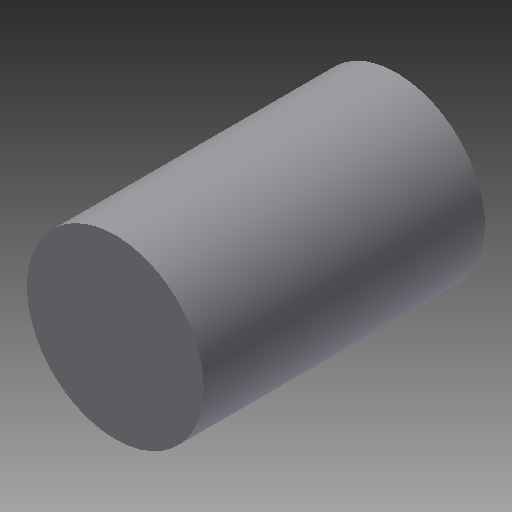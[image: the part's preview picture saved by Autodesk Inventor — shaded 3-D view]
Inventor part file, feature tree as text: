
AUTODESK INVENTOR PART (.ipt)
format: ipt  version: 2017 (Build 210142000, 142)  size: 98,304 bytes
history: native  units: in
note: dims shown in document units (in); Inventor stores cm internally (conversion verified against a paired STEP export)
features: plane x1, extrude x1, sketch x1, reference x1
ambient origin geometry x8: Origin, YZ Plane, XZ Plane, XY Plane, X Axis, Y Axis, Z Axis, Center Point
bodies: Solid1 (feature_tree)
feature tree (4):
  plane  "Work Plane1"
  extrude  "Extrusion1"  Depth=3.358in TaperAngle=0.0deg
  sketch  "Sketch1"  dims[d0=2.11in d1=3.358in d2=0.0in]
  reference  "Reference1"
